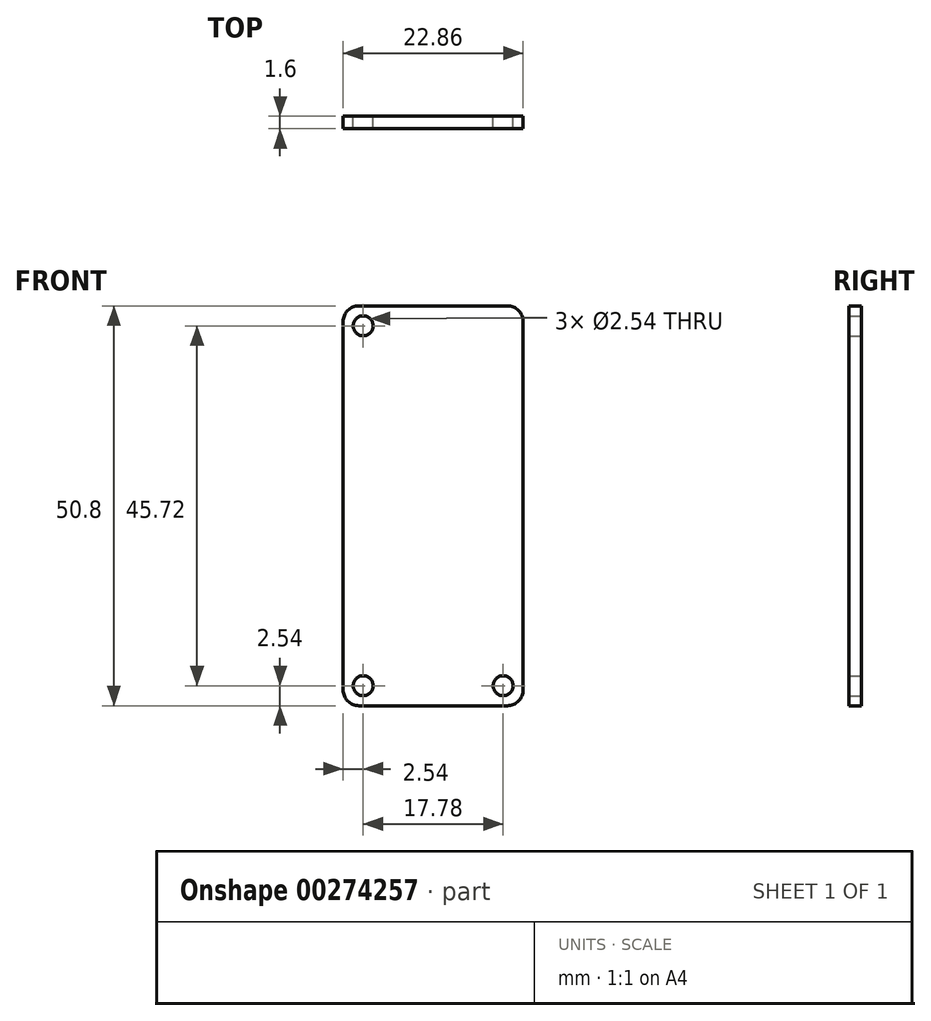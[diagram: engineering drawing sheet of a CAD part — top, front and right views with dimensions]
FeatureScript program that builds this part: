
annotation { "Feature Type Name" : "Feature", "Feature Type Description" : "" }
export const myFeature = defineFeature(function(context is Context, id is Id, definition is map)
    precondition{}
    {
        {
            var Q0;
            Q0=qCreatedBy(makeId("Front.planeOp"),FACE);
            var sketch = newSketch(context, id + "F0", { "sketchPlane" : qUnion([Q0])});
            skLineSegment(sketch, "E0.bottom", {"start": v(9.43, -25.4) * mm, "end": v(-9.43, -25.4) * mm});
            skLineSegment(sketch, "E0.top", {"start": v(9.43, 25.4) * mm, "end": v(-9.43, 25.4) * mm});
            skLineSegment(sketch, "E0.left", {"start": v(11.43, -23.4) * mm, "end": v(11.43, 23.4) * mm});
            skLineSegment(sketch, "E0.right", {"start": v(-11.43, -23.4) * mm, "end": v(-11.43, 23.4) * mm});
            skPoint(sketch, "E0.middle", {"position": v(0, 0) * mm});
            skCircle(sketch, "E1", {"center": v(8.9, -22.86) * mm, "radius": 1.27 * mm});
            skLineSegment(sketch, "E2", {"start": v(8.9, -22.86) * mm, "end": v(11.43, -22.86) * mm, "construction": true});
            skCircle(sketch, "E3", {"center": v(-8.9, -22.86) * mm, "radius": 1.27 * mm});
            skLineSegment(sketch, "E4", {"start": v(8.9, -22.86) * mm, "end": v(8.9, -25.4) * mm, "construction": true});
            skLineSegment(sketch, "E5", {"start": v(-8.9, -22.86) * mm, "end": v(-8.9, -25.4) * mm, "construction": true});
            skLineSegment(sketch, "E6", {"start": v(-8.9, -22.86) * mm, "end": v(-11.43, -22.86) * mm, "construction": true});
            skCircle(sketch, "E7", {"center": v(-8.9, 22.86) * mm, "radius": 1.27 * mm});
            skLineSegment(sketch, "E8", {"start": v(-8.9, 22.86) * mm, "end": v(-11.43, 22.86) * mm, "construction": true});
            skPoint(sketch, "E9.visualSharp", {"position": v(-11.43, 25.4) * mm});
            skArc(sketch, "E9.filletArc", {"start": v(-9.43, 25.4) * mm, "mid": v(-10.84, 24.81) * mm, "end": v(-11.43, 23.4) * mm});
            skPoint(sketch, "E10.visualSharp", {"position": v(11.43, 25.4) * mm});
            skArc(sketch, "E10.filletArc", {"start": v(11.43, 23.4) * mm, "mid": v(10.84, 24.81) * mm, "end": v(9.43, 25.4) * mm});
            skPoint(sketch, "E11.visualSharp", {"position": v(11.43, -25.4) * mm});
            skArc(sketch, "E11.filletArc", {"start": v(9.43, -25.4) * mm, "mid": v(10.84, -24.81) * mm, "end": v(11.43, -23.4) * mm});
            skPoint(sketch, "E12.visualSharp", {"position": v(-11.43, -25.4) * mm});
            skArc(sketch, "E12.filletArc", {"start": v(-11.43, -23.4) * mm, "mid": v(-10.84, -24.81) * mm, "end": v(-9.43, -25.4) * mm});
            skPoint(sketch, "E13.middle", {"position": v(0, -22.67) * mm});
            skLineSegment(sketch, "E14", {"start": v(-8.9, 22.86) * mm, "end": v(-8.9, 25.4) * mm, "construction": true});
            skSolve(sketch);
        }
        {
            var Q0;
            Q0=qSketchRegion(id+"F0",true);
            extrude(context, id + "F1", {"entities" : qUnion([Q0]), "endBound" : BoundingType.SYMMETRIC, "depth" : 1.6 * mm});
        }
    });
